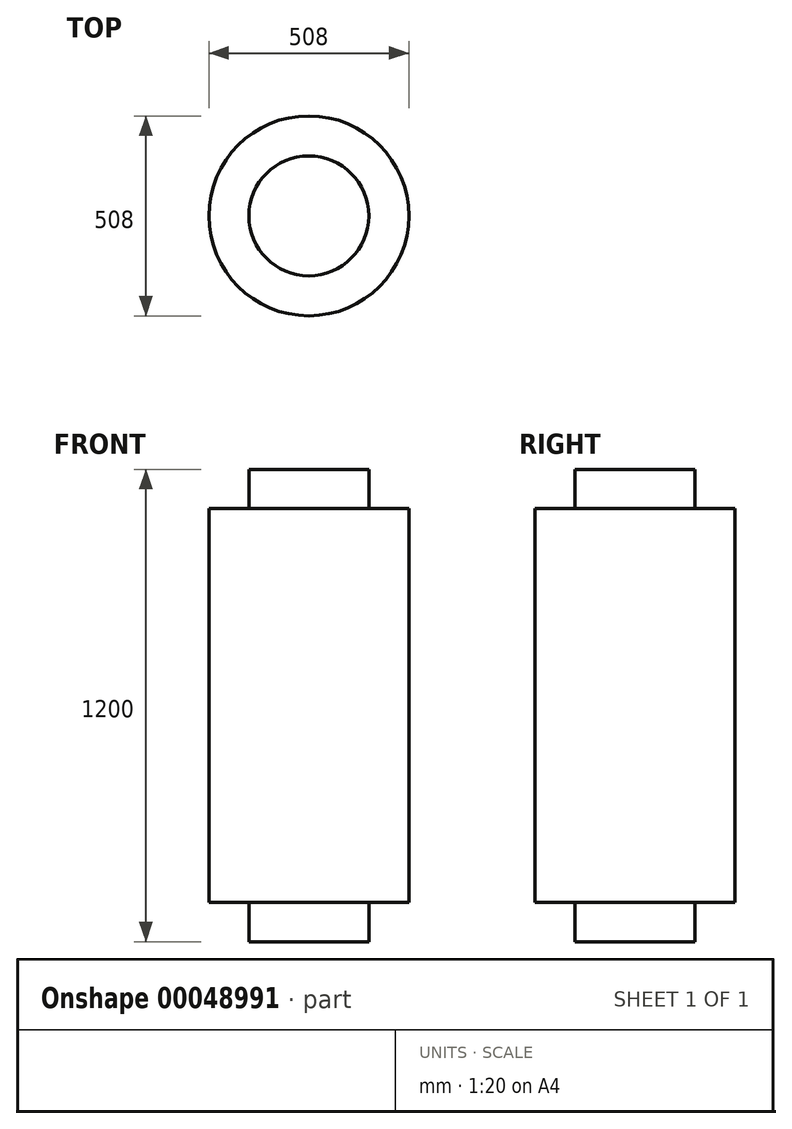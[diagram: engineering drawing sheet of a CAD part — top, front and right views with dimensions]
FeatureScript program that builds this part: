
annotation { "Feature Type Name" : "Feature", "Feature Type Description" : "" }
export const myFeature = defineFeature(function(context is Context, id is Id, definition is map)
    precondition{}
    {
        {
            var Q0;
            Q0=qCreatedBy(makeId("Top.planeOp"),FACE);
            var sketch = newSketch(context, id + "F0", { "sketchPlane" : qUnion([Q0])});
            skCircle(sketch, "E0", {"center": v(0, 0) * mm, "radius": 152.4 * mm});
            skSolve(sketch);
        }
        {
            var Q0;
            Q0 = qSketchRegion(id + "F0", true);
            extrude(context, id + "F1", {"entities" : qUnion([Q0]), "depth" : 100 * mm});
        }
        {
            var Q0;
            Q0=makeQuery(id+"F1.opExtrude","CAP_FACE",FACE,{"disambiguationData":[OSD([sQuery(id+"F0.wireOp",EDGE,"E0")])],"isStart":true});
            var sketch = newSketch(context, id + "F2", { "sketchPlane" : qUnion([Q0])});
            skCircle(sketch, "E1", {"center": v(0, 0) * mm, "radius": 254 * mm});
            skSolve(sketch);
        }
        {
            var Q0;
            Q0=makeQuery(id+"F2.imprint","IMPRINT",FACE,{"disambiguationData":[TD([[makeQuery(id+"F2.imprint","IMPRINT",EDGE,{"derivedFrom":sQuery(id+"F2.wireOp",EDGE,"E1")}),1.0]])]});
            var Q1;
            Q1=makeQuery(id+"F2.imprint","IMPRINT",FACE,{"disambiguationData":[TD([[makeQuery(id+"F2.imprint","IMPRINT",EDGE,{"derivedFrom":makeQuery(id+"F1.opExtrude","CAP_EDGE",EDGE,{"disambiguationData":[OSD([sQuery(id+"F0.wireOp",EDGE,"E0")])],"isStart":true})}),-1.0]])]});
            extrude(context, id + "F3", {"entities" : qUnion([Q0, Q1]), "operationType" : NewBodyOperationType.ADD, "depth" : 1000 * mm});
        }
        {
            var Q0;
            Q0=makeQuery(id+"F3.opExtrude","CAP_FACE",FACE,{"disambiguationData":[OSD([sQuery(id+"F2.wireOp",EDGE,"E1")])],"isStart":false});
            var sketch = newSketch(context, id + "F4", { "sketchPlane" : qUnion([Q0])});
            skCircle(sketch, "E2", {"center": v(0, 0) * mm, "radius": 152.4 * mm});
            skSolve(sketch);
        }
        {
            var Q0;
            Q0=makeQuery(id+"F4.imprint","IMPRINT",FACE,{"disambiguationData":[TD([[makeQuery(id+"F4.imprint","IMPRINT",EDGE,{"derivedFrom":sQuery(id+"F4.wireOp",EDGE,"E2")}),1.0]])]});
            extrude(context, id + "F5", {"entities" : qUnion([Q0]), "operationType" : NewBodyOperationType.ADD, "depth" : 100 * mm});
        }
    });
